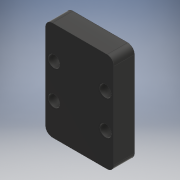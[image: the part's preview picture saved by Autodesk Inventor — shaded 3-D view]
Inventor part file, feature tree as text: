
AUTODESK INVENTOR PART (.ipt)
format: ipt  version: 2017.3 (Build 213256000, 256)  size: 117,760 bytes
history: native  units: mm
features: extrude x1, fillet x1, sketch x1
ambient origin geometry x8: Origin, YZ Plane, XZ Plane, XY Plane, X Axis, Y Axis, Z Axis, Center Point
bodies: Solid1 (feature_tree)
feature tree (3):
  extrude  "Extrusion1"  Depth=20.0mm
  fillet  "Fillet1"  Radius=15.0mm
  sketch  "Sketch1"  dims[d0=29.0mm d1=20.0mm d2=15.0mm d3=10.0mm d4=3.4mm d5=6.0mm d6=0.0mm d7=2.0mm]
